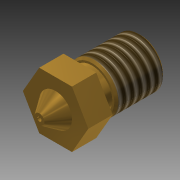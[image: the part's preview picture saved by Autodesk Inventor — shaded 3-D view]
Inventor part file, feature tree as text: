
AUTODESK INVENTOR PART (.ipt)
format: ipt  version: 2015 (Build 190159000, 159)  size: 150,528 bytes
history: native  units: mm
features: sketch x4, hole x3, chamfer x2, other x1, revolve x1, thread x1, extrude x1
ambient origin geometry x8: Origin, YZ Plane, XZ Plane, XY Plane, X Axis, Y Axis, Z Axis, Center Point
bodies: Body1 (feature_tree)
feature tree (13):
  other  "Твердое тело1"
  revolve  "Вращение1"
  chamfer  "Фаска1"  Distance=15.0mm
  thread  "Резьба1"
  sketch  "Эскиз2"
  sketch  "Эскиз3"
  hole  "Отверстие1"  [1 undecoded]
  hole  "Отверстие2"  [1 undecoded]
  chamfer  "Фаска2"  Distance=7.5mm
  hole  "Отверстие3"  [1 undecoded]
  extrude  "Выдавливание1"  Depth=5.0mm
  sketch  "Эскиз1"
  sketch  "Эскиз4"
note: 3 required parameter values undecoded (feature->parameter linkage not recoverable at this tier; creation-order binding heuristic only, values carry confidence <= 0.55)
